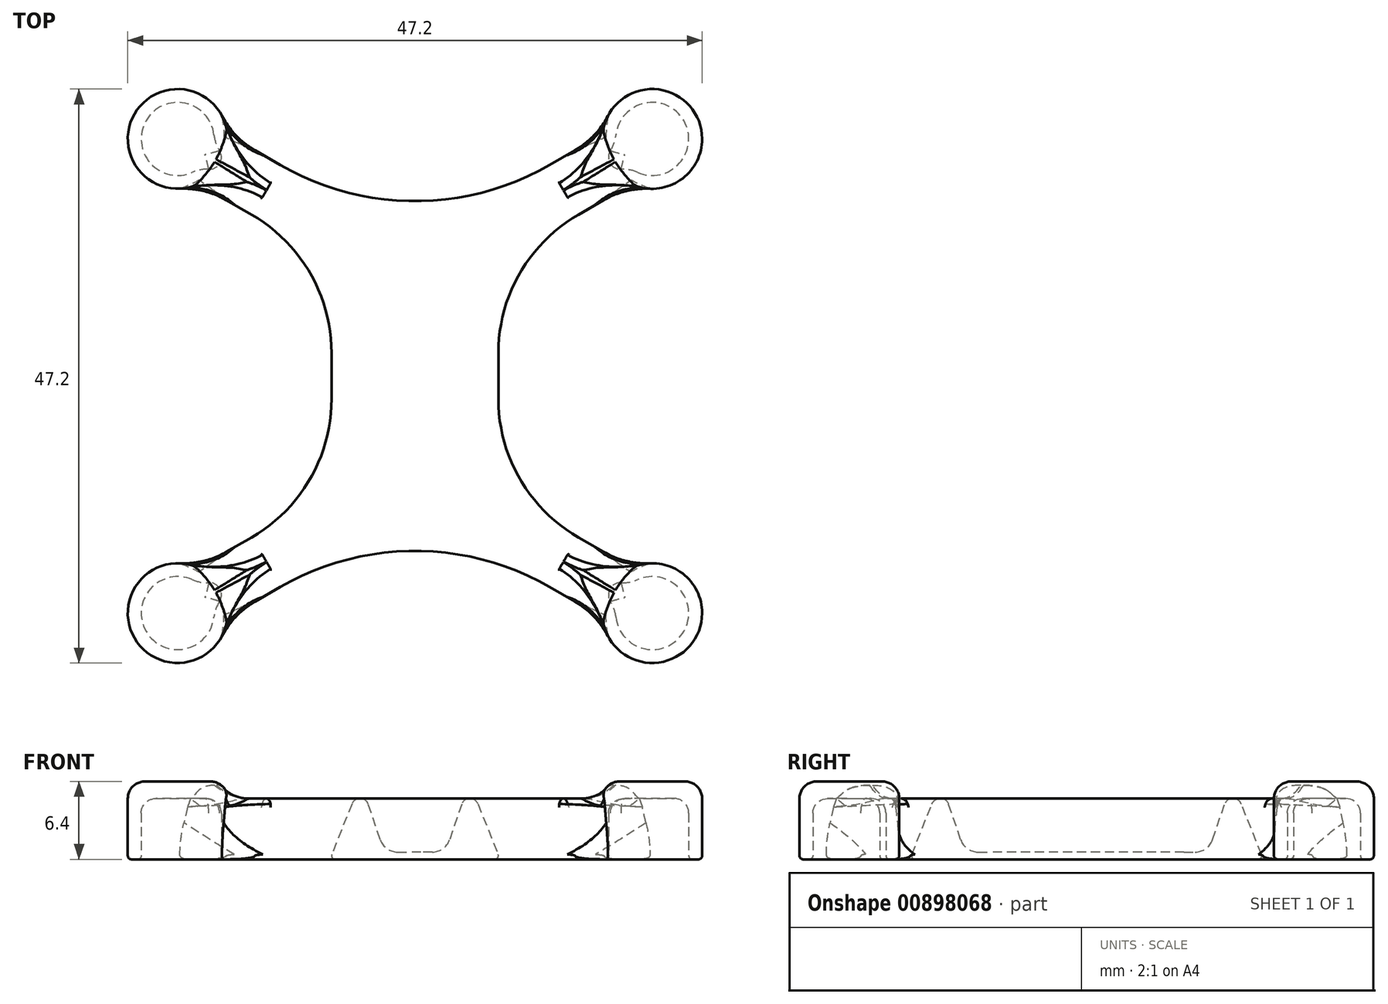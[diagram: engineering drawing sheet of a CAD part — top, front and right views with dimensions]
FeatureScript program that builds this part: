
annotation { "Feature Type Name" : "Feature", "Feature Type Description" : "" }
export const myFeature = defineFeature(function(context is Context, id is Id, definition is map)
    precondition{}
    {
        {
            var Q0;
            Q0=qCreatedBy(makeId("Top.planeOp"),FACE);
            var sketch = newSketch(context, id + "F0", { "sketchPlane" : qUnion([Q0])});
            skLineSegment(sketch, "E0", {"start": v(-15.44, 20.04) * mm, "end": v(0, 11.13) * mm});
            skLineSegment(sketch, "E1", {"start": v(0, 11.13) * mm, "end": v(15.44, 20.04) * mm});
            skLineSegment(sketch, "E2", {"start": v(-15.44, -20.04) * mm, "end": v(0, -11.13) * mm});
            skLineSegment(sketch, "E3", {"start": v(0, -11.13) * mm, "end": v(15.44, -20.04) * mm});
            skLineSegment(sketch, "E4", {"start": v(-17.94, 15.71) * mm, "end": v(-7, 9.4) * mm});
            skLineSegment(sketch, "E5", {"start": v(-7, 9.4) * mm, "end": v(-7, -9.4) * mm});
            skLineSegment(sketch, "E6", {"start": v(-7, -9.4) * mm, "end": v(-17.94, -15.71) * mm});
            skLineSegment(sketch, "E7", {"start": v(17.94, -15.71) * mm, "end": v(7, -9.4) * mm});
            skLineSegment(sketch, "E8", {"start": v(7, -9.4) * mm, "end": v(7, 9.4) * mm});
            skLineSegment(sketch, "E9", {"start": v(7, 9.4) * mm, "end": v(17.94, 15.71) * mm});
            skArc(sketch, "E10", {"start": v(-17.94, 15.71) * mm, "mid": v(-23.05, 21.55) * mm, "end": v(-15.44, 20.04) * mm});
            skArc(sketch, "E11", {"start": v(17.94, 15.71) * mm, "mid": v(23.05, 21.55) * mm, "end": v(15.44, 20.04) * mm});
            skArc(sketch, "E12", {"start": v(17.94, -15.71) * mm, "mid": v(23.05, -21.55) * mm, "end": v(15.44, -20.04) * mm});
            skArc(sketch, "E13", {"start": v(-17.94, -15.71) * mm, "mid": v(-23.05, -21.55) * mm, "end": v(-15.44, -20.04) * mm});
            skArc(sketch, "E14", {"start": v(-16.06, 18.54) * mm, "mid": v(-16.04, 17.5) * mm, "end": v(-16.95, 17) * mm});
            skArc(sketch, "E15", {"start": v(16.06, 18.54) * mm, "mid": v(16.04, 17.5) * mm, "end": v(16.95, 17) * mm});
            skArc(sketch, "E16", {"start": v(-16.95, -17) * mm, "mid": v(-16.04, -17.5) * mm, "end": v(-16.06, -18.54) * mm});
            skArc(sketch, "E17", {"start": v(16.95, -17) * mm, "mid": v(16.04, -17.5) * mm, "end": v(16.06, -18.54) * mm});
            skArc(sketch, "E18", {"start": v(18.3, -16.75) * mm, "mid": v(22.1, -21) * mm, "end": v(16.52, -19.83) * mm});
            skArc(sketch, "E19", {"start": v(-18.3, -16.75) * mm, "mid": v(-22.1, -21) * mm, "end": v(-16.52, -19.83) * mm});
            skArc(sketch, "E20", {"start": v(-16.52, 19.83) * mm, "mid": v(-22.1, 21) * mm, "end": v(-18.3, 16.75) * mm});
            skArc(sketch, "E21", {"start": v(18.3, 16.75) * mm, "mid": v(22.1, 21) * mm, "end": v(16.52, 19.83) * mm});
            skPoint(sketch, "E22.visualSharp", {"position": v(-16.55, 18.94) * mm});
            skArc(sketch, "E22.filletArc", {"start": v(-16.52, 19.83) * mm, "mid": v(-16.36, 19.16) * mm, "end": v(-16.06, 18.54) * mm});
            skPoint(sketch, "E23.visualSharp", {"position": v(-17.54, 17.23) * mm});
            skArc(sketch, "E23.filletArc", {"start": v(-16.95, 17) * mm, "mid": v(-17.64, 16.95) * mm, "end": v(-18.3, 16.75) * mm});
            skPoint(sketch, "E24.visualSharp", {"position": v(16.55, 18.94) * mm});
            skArc(sketch, "E24.filletArc", {"start": v(16.06, 18.54) * mm, "mid": v(16.36, 19.16) * mm, "end": v(16.52, 19.83) * mm});
            skPoint(sketch, "E25.visualSharp", {"position": v(17.54, 17.23) * mm});
            skArc(sketch, "E25.filletArc", {"start": v(18.3, 16.75) * mm, "mid": v(17.64, 16.95) * mm, "end": v(16.95, 17) * mm});
            skPoint(sketch, "E26.visualSharp", {"position": v(17.54, -17.23) * mm});
            skArc(sketch, "E26.filletArc", {"start": v(16.95, -17) * mm, "mid": v(17.64, -16.95) * mm, "end": v(18.3, -16.75) * mm});
            skPoint(sketch, "E27.visualSharp", {"position": v(16.55, -18.94) * mm});
            skArc(sketch, "E27.filletArc", {"start": v(16.52, -19.83) * mm, "mid": v(16.36, -19.16) * mm, "end": v(16.06, -18.54) * mm});
            skPoint(sketch, "E28.visualSharp", {"position": v(-17.54, -17.23) * mm});
            skArc(sketch, "E28.filletArc", {"start": v(-18.3, -16.75) * mm, "mid": v(-17.64, -16.95) * mm, "end": v(-16.95, -17) * mm});
            skPoint(sketch, "E29.visualSharp", {"position": v(-16.55, -18.94) * mm});
            skArc(sketch, "E29.filletArc", {"start": v(-16.06, -18.54) * mm, "mid": v(-16.36, -19.16) * mm, "end": v(-16.52, -19.83) * mm});
            skSolve(sketch);
        }
        {
            var Q0;
            Q0=qSketchRegion(id+"F0",true);
            extrude(context, id + "F1", {"entities" : qUnion([Q0]), "depth" : 5 * mm, "offsetDistance" : 25 * mm});
        }
        {
            var Q0;
            Q0=qCreatedBy(makeId("Front.planeOp"),FACE);
            var sketch = newSketch(context, id + "F2", { "sketchPlane" : qUnion([Q0])});
            skLineSegment(sketch, "E30.bottom", {"start": v(-2.5, 5.6) * mm, "end": v(2.5, 5.6) * mm});
            skLineSegment(sketch, "E30.top", {"start": v(-2.5, 0.6) * mm, "end": v(2.5, 0.6) * mm});
            skLineSegment(sketch, "E30.left", {"start": v(-2.5, 5.6) * mm, "end": v(-2.5, 0.6) * mm});
            skLineSegment(sketch, "E30.right", {"start": v(2.5, 5.6) * mm, "end": v(2.5, 0.6) * mm});
            skSolve(sketch);
        }
        {
            var Q0;
            Q0=qSketchRegion(id+"F2",true);
            extrude(context, id + "F3", {"entities" : qUnion([Q0]), "operationType" : NewBodyOperationType.REMOVE, "oppositeDirection" : true, "depth" : 10 * mm, "offsetDistance" : 25 * mm, "hasSecondDirection" : true, "secondDirectionOppositeDirection" : false, "secondDirectionDepth" : 10 * mm});
        }
        {
            var Q0;
            Q0=makeQuery(id+"F1.opExtrude","CAP_FACE",FACE,{"disambiguationData":[OSD([sQuery(id+"F0.wireOp",EDGE,"E0"),sQuery(id+"F0.wireOp",EDGE,"E1"),sQuery(id+"F0.wireOp",EDGE,"E2"),sQuery(id+"F0.wireOp",EDGE,"E3"),sQuery(id+"F0.wireOp",EDGE,"E4"),sQuery(id+"F0.wireOp",EDGE,"E5"),sQuery(id+"F0.wireOp",EDGE,"E6"),sQuery(id+"F0.wireOp",EDGE,"E7"),sQuery(id+"F0.wireOp",EDGE,"E8"),sQuery(id+"F0.wireOp",EDGE,"E9"),sQuery(id+"F0.wireOp",EDGE,"E10"),sQuery(id+"F0.wireOp",EDGE,"E11"),sQuery(id+"F0.wireOp",EDGE,"E12"),sQuery(id+"F0.wireOp",EDGE,"E13"),sQuery(id+"F0.wireOp",EDGE,"E14"),sQuery(id+"F0.wireOp",EDGE,"E15"),sQuery(id+"F0.wireOp",EDGE,"E16"),sQuery(id+"F0.wireOp",EDGE,"E17"),sQuery(id+"F0.wireOp",EDGE,"E18"),sQuery(id+"F0.wireOp",EDGE,"E19"),sQuery(id+"F0.wireOp",EDGE,"E20"),sQuery(id+"F0.wireOp",EDGE,"E21")])],"isStart":false});
            var sketch = newSketch(context, id + "F4", { "sketchPlane" : qUnion([Q0])});
            skCircle(sketch, "E31", {"center": v(-19.5, 19.5) * mm, "radius": 4.1 * mm});
            skCircle(sketch, "E32", {"center": v(19.5, 19.5) * mm, "radius": 4.1 * mm});
            skCircle(sketch, "E33", {"center": v(19.5, -19.5) * mm, "radius": 4.1 * mm});
            skCircle(sketch, "E34", {"center": v(-19.5, -19.5) * mm, "radius": 4.1 * mm});
            skSolve(sketch);
        }
        {
            var Q0;
            Q0=qSketchRegion(id+"F4",true);
            extrude(context, id + "F5", {"entities" : qUnion([Q0]), "operationType" : NewBodyOperationType.ADD, "depth" : 1.4 * mm, "offsetDistance" : 25 * mm});
        }
        {
            var Q0;
            Q0=makeQuery(id+"F1.opExtrude","SWEPT_EDGE",EDGE,{"disambiguationData":[OSD([sQuery(id+"F0.wireOp",EDGE,"E0"),sQuery(id+"F0.wireOp",EDGE,"E1")])]});
            var Q1;
            Q1=makeQuery(id+"F1.opExtrude","SWEPT_EDGE",EDGE,{"disambiguationData":[OSD([sQuery(id+"F0.wireOp",EDGE,"E2"),sQuery(id+"F0.wireOp",EDGE,"E3")])]});
            fillet(context, id + "F6", {"entities" : qUnion([Q0, Q1]), "radius" : 22 * mm, "tangentPropagation" : true, "allowEdgeOverflow" : false});
        }
        {
            var Q0;
            Q0=makeQuery(id+"F1.opExtrude","SWEPT_EDGE",EDGE,{"disambiguationData":[OSD([sQuery(id+"F0.wireOp",EDGE,"E4"),sQuery(id+"F0.wireOp",EDGE,"E5")])]});
            var Q1;
            Q1=makeQuery(id+"F1.opExtrude","SWEPT_EDGE",EDGE,{"disambiguationData":[OSD([sQuery(id+"F0.wireOp",EDGE,"E5"),sQuery(id+"F0.wireOp",EDGE,"E6")])]});
            var Q2;
            Q2=makeQuery(id+"F1.opExtrude","SWEPT_EDGE",EDGE,{"disambiguationData":[OSD([sQuery(id+"F0.wireOp",EDGE,"E8"),sQuery(id+"F0.wireOp",EDGE,"E9")])]});
            var Q3;
            Q3=makeQuery(id+"F1.opExtrude","SWEPT_EDGE",EDGE,{"disambiguationData":[OSD([sQuery(id+"F0.wireOp",EDGE,"E7"),sQuery(id+"F0.wireOp",EDGE,"E8")])]});
            fillet(context, id + "F7", {"entities" : qUnion([Q0, Q1, Q2, Q3]), "radius" : 13 * mm, "tangentPropagation" : true, "allowEdgeOverflow" : false});
        }
        {
            var Q0;
            Q0=makeQuery(id+"F1.opExtrude","CAP_EDGE",EDGE,{"disambiguationData":[OSD([sQuery(id+"F0.wireOp",EDGE,"E2")])],"isStart":false});
            var Q1;
            Q1=makeQuery(id+"F1.opExtrude","CAP_EDGE",EDGE,{"disambiguationData":[OSD([sQuery(id+"F0.wireOp",EDGE,"E6")])],"isStart":false});
            var Q2;
            Q2=makeQuery(id+"F1.opExtrude","CAP_EDGE",EDGE,{"disambiguationData":[OSD([sQuery(id+"F0.wireOp",EDGE,"E3")])],"isStart":false});
            var Q3;
            Q3=makeQuery(id+"F1.opExtrude","CAP_EDGE",EDGE,{"disambiguationData":[OSD([sQuery(id+"F0.wireOp",EDGE,"E7")])],"isStart":false});
            var Q4;
            Q4=makeQuery(id+"F1.opExtrude","CAP_EDGE",EDGE,{"disambiguationData":[OSD([sQuery(id+"F0.wireOp",EDGE,"E1")])],"isStart":false});
            var Q5;
            Q5=makeQuery(id+"F1.opExtrude","CAP_EDGE",EDGE,{"disambiguationData":[OSD([sQuery(id+"F0.wireOp",EDGE,"E0")])],"isStart":false});
            var Q6;
            Q6=makeQuery(id+"F1.opExtrude","CAP_EDGE",EDGE,{"disambiguationData":[OSD([sQuery(id+"F0.wireOp",EDGE,"E4")])],"isStart":false});
            var Q7;
            Q7=makeQuery(id+"F1.opExtrude","CAP_EDGE",EDGE,{"disambiguationData":[OSD([sQuery(id+"F0.wireOp",EDGE,"E9")])],"isStart":false});
            chamfer(context, id + "F8", {"entities" : qUnion([Q0, Q1, Q2, Q3, Q4, Q5, Q6, Q7]), "chamferType" : ChamferType.TWO_OFFSETS, "width1" : 2 * mm, "oppositeDirection" : false, "width2" : 5 * mm, "tangentPropagation" : true});
        }
        {
            var Q0;
            Q0=makeQuery(id+"F3.boolean.opBoolean","COPY",EDGE,{"derivedFrom":makeQuery(id+"F3.opExtrude","CAP_EDGE",EDGE,{"disambiguationData":[OSD([sQuery(id+"F2.wireOp",EDGE,"E30.left")])],"isStart":false})});
            var Q1;
            Q1=makeQuery(id+"F3.boolean.opBoolean","COPY",EDGE,{"derivedFrom":makeQuery(id+"F3.opExtrude","CAP_EDGE",EDGE,{"disambiguationData":[OSD([sQuery(id+"F2.wireOp",EDGE,"E30.right")])],"isStart":false})});
            var Q2;
            Q2=makeQuery(id+"F3.boolean.opBoolean","COPY",EDGE,{"derivedFrom":makeQuery(id+"F3.opExtrude","CAP_EDGE",EDGE,{"disambiguationData":[OSD([sQuery(id+"F2.wireOp",EDGE,"E30.left")])],"isStart":true})});
            var Q3;
            Q3=makeQuery(id+"F3.boolean.opBoolean","COPY",EDGE,{"derivedFrom":makeQuery(id+"F3.opExtrude","CAP_EDGE",EDGE,{"disambiguationData":[OSD([sQuery(id+"F2.wireOp",EDGE,"E30.right")])],"isStart":true})});
            fillet(context, id + "F9", {"entities" : qUnion([Q0, Q1, Q2, Q3]), "radius" : 2 * mm, "tangentPropagation" : true, "allowEdgeOverflow" : false});
        }
        {
            var Q0;
            Q0=makeQuery(id+"F3.boolean.opBoolean","INTERSECT",EDGE,{"derivedFrom":[makeQuery(id+"F1.opExtrude","CAP_FACE",FACE,{"disambiguationData":[OSD([sQuery(id+"F0.wireOp",EDGE,"E0"),sQuery(id+"F0.wireOp",EDGE,"E1"),sQuery(id+"F0.wireOp",EDGE,"E2"),sQuery(id+"F0.wireOp",EDGE,"E3"),sQuery(id+"F0.wireOp",EDGE,"E4"),sQuery(id+"F0.wireOp",EDGE,"E5"),sQuery(id+"F0.wireOp",EDGE,"E6"),sQuery(id+"F0.wireOp",EDGE,"E7"),sQuery(id+"F0.wireOp",EDGE,"E8"),sQuery(id+"F0.wireOp",EDGE,"E9"),sQuery(id+"F0.wireOp",EDGE,"E10"),sQuery(id+"F0.wireOp",EDGE,"E11"),sQuery(id+"F0.wireOp",EDGE,"E12"),sQuery(id+"F0.wireOp",EDGE,"E13"),sQuery(id+"F0.wireOp",EDGE,"E14"),sQuery(id+"F0.wireOp",EDGE,"E15"),sQuery(id+"F0.wireOp",EDGE,"E16"),sQuery(id+"F0.wireOp",EDGE,"E17"),sQuery(id+"F0.wireOp",EDGE,"E18"),sQuery(id+"F0.wireOp",EDGE,"E19"),sQuery(id+"F0.wireOp",EDGE,"E20"),sQuery(id+"F0.wireOp",EDGE,"E21"),sQuery(id+"F0.wireOp",EDGE,"E22.filletArc"),sQuery(id+"F0.wireOp",EDGE,"E23.filletArc"),sQuery(id+"F0.wireOp",EDGE,"E24.filletArc"),sQuery(id+"F0.wireOp",EDGE,"E25.filletArc"),sQuery(id+"F0.wireOp",EDGE,"E26.filletArc"),sQuery(id+"F0.wireOp",EDGE,"E27.filletArc"),sQuery(id+"F0.wireOp",EDGE,"E28.filletArc"),sQuery(id+"F0.wireOp",EDGE,"E29.filletArc")])],"isStart":false}),makeQuery(id+"F3.opExtrude","CAP_FACE",FACE,{"disambiguationData":[OSD([sQuery(id+"F2.wireOp",EDGE,"E30.bottom"),sQuery(id+"F2.wireOp",EDGE,"E30.top"),sQuery(id+"F2.wireOp",EDGE,"E30.left"),sQuery(id+"F2.wireOp",EDGE,"E30.right")])],"isStart":false})]});
            chamfer(context, id + "F10", {"entities" : qUnion([Q0]), "chamferType" : ChamferType.TWO_OFFSETS, "width1" : 1.5 * mm, "oppositeDirection" : false, "width2" : 4.4 * mm, "tangentPropagation" : true});
        }
        {
            var Q0;
            Q0=makeQuery(id+"F5.opExtrude","CAP_FACE",FACE,{"disambiguationData":[OSD([sQuery(id+"F4.wireOp",EDGE,"E34")])],"isStart":true});
            var Q1;
            Q1=makeQuery(id+"F5.opExtrude","CAP_FACE",FACE,{"disambiguationData":[OSD([sQuery(id+"F4.wireOp",EDGE,"E33")])],"isStart":true});
            var Q2;
            Q2=makeQuery(id+"F5.opExtrude","CAP_FACE",FACE,{"disambiguationData":[OSD([sQuery(id+"F4.wireOp",EDGE,"E32")])],"isStart":true});
            var Q3;
            Q3=makeQuery(id+"F5.opExtrude","CAP_FACE",FACE,{"disambiguationData":[OSD([sQuery(id+"F4.wireOp",EDGE,"E31")])],"isStart":true});
            fillet(context, id + "F11", {"entities" : qUnion([Q0, Q1, Q2, Q3]), "radius" : 1.2 * mm, "tangentPropagation" : true, "allowEdgeOverflow" : false});
        }
        {
            var Q0;
            Q0=makeQuery(id+"F1.opExtrude","CAP_FACE",FACE,{"disambiguationData":[OSD([sQuery(id+"F0.wireOp",EDGE,"E0"),sQuery(id+"F0.wireOp",EDGE,"E1"),sQuery(id+"F0.wireOp",EDGE,"E2"),sQuery(id+"F0.wireOp",EDGE,"E3"),sQuery(id+"F0.wireOp",EDGE,"E4"),sQuery(id+"F0.wireOp",EDGE,"E5"),sQuery(id+"F0.wireOp",EDGE,"E6"),sQuery(id+"F0.wireOp",EDGE,"E7"),sQuery(id+"F0.wireOp",EDGE,"E8"),sQuery(id+"F0.wireOp",EDGE,"E9"),sQuery(id+"F0.wireOp",EDGE,"E10"),sQuery(id+"F0.wireOp",EDGE,"E11"),sQuery(id+"F0.wireOp",EDGE,"E12"),sQuery(id+"F0.wireOp",EDGE,"E13"),sQuery(id+"F0.wireOp",EDGE,"E14"),sQuery(id+"F0.wireOp",EDGE,"E15"),sQuery(id+"F0.wireOp",EDGE,"E16"),sQuery(id+"F0.wireOp",EDGE,"E17"),sQuery(id+"F0.wireOp",EDGE,"E18"),sQuery(id+"F0.wireOp",EDGE,"E19"),sQuery(id+"F0.wireOp",EDGE,"E20"),sQuery(id+"F0.wireOp",EDGE,"E21"),sQuery(id+"F0.wireOp",EDGE,"E22.filletArc"),sQuery(id+"F0.wireOp",EDGE,"E23.filletArc"),sQuery(id+"F0.wireOp",EDGE,"E24.filletArc"),sQuery(id+"F0.wireOp",EDGE,"E25.filletArc"),sQuery(id+"F0.wireOp",EDGE,"E26.filletArc"),sQuery(id+"F0.wireOp",EDGE,"E27.filletArc"),sQuery(id+"F0.wireOp",EDGE,"E28.filletArc"),sQuery(id+"F0.wireOp",EDGE,"E29.filletArc")])],"isStart":true});
            var Q1;
            {var subQ0=sQuery(id+"F0.wireOp",EDGE,"E3");var subQ1=sQuery(id+"F0.wireOp",EDGE,"E2");Q1=makeQuery(id+"F8.opChamfer","BLEND_EDGE",EDGE,{"blendedFrom":[makeQuery(id+"F6.opFillet","BLEND_EDGE",EDGE,{"blendedFrom":[makeQuery(id+"F1.opExtrude","SWEPT_EDGE",EDGE,{"disambiguationData":[OSD([subQ1,subQ0])]}),makeQuery(id+"F1.opExtrude","CAP_FACE",FACE,{"disambiguationData":[OSD([sQuery(id+"F0.wireOp",EDGE,"E0"),sQuery(id+"F0.wireOp",EDGE,"E1"),subQ1,subQ0,sQuery(id+"F0.wireOp",EDGE,"E4"),sQuery(id+"F0.wireOp",EDGE,"E5"),sQuery(id+"F0.wireOp",EDGE,"E6"),sQuery(id+"F0.wireOp",EDGE,"E7"),sQuery(id+"F0.wireOp",EDGE,"E8"),sQuery(id+"F0.wireOp",EDGE,"E9"),sQuery(id+"F0.wireOp",EDGE,"E10"),sQuery(id+"F0.wireOp",EDGE,"E11"),sQuery(id+"F0.wireOp",EDGE,"E12"),sQuery(id+"F0.wireOp",EDGE,"E13"),sQuery(id+"F0.wireOp",EDGE,"E14"),sQuery(id+"F0.wireOp",EDGE,"E15"),sQuery(id+"F0.wireOp",EDGE,"E16"),sQuery(id+"F0.wireOp",EDGE,"E17"),sQuery(id+"F0.wireOp",EDGE,"E18"),sQuery(id+"F0.wireOp",EDGE,"E19"),sQuery(id+"F0.wireOp",EDGE,"E20"),sQuery(id+"F0.wireOp",EDGE,"E21"),sQuery(id+"F0.wireOp",EDGE,"E22.filletArc"),sQuery(id+"F0.wireOp",EDGE,"E23.filletArc"),sQuery(id+"F0.wireOp",EDGE,"E24.filletArc"),sQuery(id+"F0.wireOp",EDGE,"E25.filletArc"),sQuery(id+"F0.wireOp",EDGE,"E26.filletArc"),sQuery(id+"F0.wireOp",EDGE,"E27.filletArc"),sQuery(id+"F0.wireOp",EDGE,"E28.filletArc"),sQuery(id+"F0.wireOp",EDGE,"E29.filletArc")])],"isStart":false})],"blendedInto":[makeQuery(id+"F1.opExtrude","CAP_FACE",FACE,{"disambiguationData":[OSD([sQuery(id+"F0.wireOp",EDGE,"E0"),sQuery(id+"F0.wireOp",EDGE,"E1"),subQ1,subQ0,sQuery(id+"F0.wireOp",EDGE,"E4"),sQuery(id+"F0.wireOp",EDGE,"E5"),sQuery(id+"F0.wireOp",EDGE,"E6"),sQuery(id+"F0.wireOp",EDGE,"E7"),sQuery(id+"F0.wireOp",EDGE,"E8"),sQuery(id+"F0.wireOp",EDGE,"E9"),sQuery(id+"F0.wireOp",EDGE,"E10"),sQuery(id+"F0.wireOp",EDGE,"E11"),sQuery(id+"F0.wireOp",EDGE,"E12"),sQuery(id+"F0.wireOp",EDGE,"E13"),sQuery(id+"F0.wireOp",EDGE,"E14"),sQuery(id+"F0.wireOp",EDGE,"E15"),sQuery(id+"F0.wireOp",EDGE,"E16"),sQuery(id+"F0.wireOp",EDGE,"E17"),sQuery(id+"F0.wireOp",EDGE,"E18"),sQuery(id+"F0.wireOp",EDGE,"E19"),sQuery(id+"F0.wireOp",EDGE,"E20"),sQuery(id+"F0.wireOp",EDGE,"E21"),sQuery(id+"F0.wireOp",EDGE,"E22.filletArc"),sQuery(id+"F0.wireOp",EDGE,"E23.filletArc"),sQuery(id+"F0.wireOp",EDGE,"E24.filletArc"),sQuery(id+"F0.wireOp",EDGE,"E25.filletArc"),sQuery(id+"F0.wireOp",EDGE,"E26.filletArc"),sQuery(id+"F0.wireOp",EDGE,"E27.filletArc"),sQuery(id+"F0.wireOp",EDGE,"E28.filletArc"),sQuery(id+"F0.wireOp",EDGE,"E29.filletArc")])],"isStart":false})]}),makeQuery(id+"F6.opFillet","BLEND_FACE",FACE,{"disambiguationData":[OSD([subQ1,subQ0])]})],"blendedInto":[makeQuery(id+"F6.opFillet","BLEND_FACE",FACE,{"disambiguationData":[OSD([subQ1,subQ0])]})]});}
            var Q2;
            {var subQ0=sQuery(id+"F0.wireOp",EDGE,"E5");var subQ1=sQuery(id+"F0.wireOp",EDGE,"E4");Q2=makeQuery(id+"F8.opChamfer","BLEND_EDGE",EDGE,{"blendedFrom":[makeQuery(id+"F7.opFillet","BLEND_EDGE",EDGE,{"blendedFrom":[makeQuery(id+"F1.opExtrude","SWEPT_EDGE",EDGE,{"disambiguationData":[OSD([subQ1,subQ0])]}),makeQuery(id+"F1.opExtrude","CAP_FACE",FACE,{"disambiguationData":[OSD([sQuery(id+"F0.wireOp",EDGE,"E0"),sQuery(id+"F0.wireOp",EDGE,"E1"),sQuery(id+"F0.wireOp",EDGE,"E2"),sQuery(id+"F0.wireOp",EDGE,"E3"),subQ1,subQ0,sQuery(id+"F0.wireOp",EDGE,"E6"),sQuery(id+"F0.wireOp",EDGE,"E7"),sQuery(id+"F0.wireOp",EDGE,"E8"),sQuery(id+"F0.wireOp",EDGE,"E9"),sQuery(id+"F0.wireOp",EDGE,"E10"),sQuery(id+"F0.wireOp",EDGE,"E11"),sQuery(id+"F0.wireOp",EDGE,"E12"),sQuery(id+"F0.wireOp",EDGE,"E13"),sQuery(id+"F0.wireOp",EDGE,"E14"),sQuery(id+"F0.wireOp",EDGE,"E15"),sQuery(id+"F0.wireOp",EDGE,"E16"),sQuery(id+"F0.wireOp",EDGE,"E17"),sQuery(id+"F0.wireOp",EDGE,"E18"),sQuery(id+"F0.wireOp",EDGE,"E19"),sQuery(id+"F0.wireOp",EDGE,"E20"),sQuery(id+"F0.wireOp",EDGE,"E21"),sQuery(id+"F0.wireOp",EDGE,"E22.filletArc"),sQuery(id+"F0.wireOp",EDGE,"E23.filletArc"),sQuery(id+"F0.wireOp",EDGE,"E24.filletArc"),sQuery(id+"F0.wireOp",EDGE,"E25.filletArc"),sQuery(id+"F0.wireOp",EDGE,"E26.filletArc"),sQuery(id+"F0.wireOp",EDGE,"E27.filletArc"),sQuery(id+"F0.wireOp",EDGE,"E28.filletArc"),sQuery(id+"F0.wireOp",EDGE,"E29.filletArc")])],"isStart":false})],"blendedInto":[makeQuery(id+"F1.opExtrude","CAP_FACE",FACE,{"disambiguationData":[OSD([sQuery(id+"F0.wireOp",EDGE,"E0"),sQuery(id+"F0.wireOp",EDGE,"E1"),sQuery(id+"F0.wireOp",EDGE,"E2"),sQuery(id+"F0.wireOp",EDGE,"E3"),subQ1,subQ0,sQuery(id+"F0.wireOp",EDGE,"E6"),sQuery(id+"F0.wireOp",EDGE,"E7"),sQuery(id+"F0.wireOp",EDGE,"E8"),sQuery(id+"F0.wireOp",EDGE,"E9"),sQuery(id+"F0.wireOp",EDGE,"E10"),sQuery(id+"F0.wireOp",EDGE,"E11"),sQuery(id+"F0.wireOp",EDGE,"E12"),sQuery(id+"F0.wireOp",EDGE,"E13"),sQuery(id+"F0.wireOp",EDGE,"E14"),sQuery(id+"F0.wireOp",EDGE,"E15"),sQuery(id+"F0.wireOp",EDGE,"E16"),sQuery(id+"F0.wireOp",EDGE,"E17"),sQuery(id+"F0.wireOp",EDGE,"E18"),sQuery(id+"F0.wireOp",EDGE,"E19"),sQuery(id+"F0.wireOp",EDGE,"E20"),sQuery(id+"F0.wireOp",EDGE,"E21"),sQuery(id+"F0.wireOp",EDGE,"E22.filletArc"),sQuery(id+"F0.wireOp",EDGE,"E23.filletArc"),sQuery(id+"F0.wireOp",EDGE,"E24.filletArc"),sQuery(id+"F0.wireOp",EDGE,"E25.filletArc"),sQuery(id+"F0.wireOp",EDGE,"E26.filletArc"),sQuery(id+"F0.wireOp",EDGE,"E27.filletArc"),sQuery(id+"F0.wireOp",EDGE,"E28.filletArc"),sQuery(id+"F0.wireOp",EDGE,"E29.filletArc")])],"isStart":false})]}),makeQuery(id+"F7.opFillet","BLEND_FACE",FACE,{"disambiguationData":[OSD([subQ1,subQ0])]})],"blendedInto":[makeQuery(id+"F7.opFillet","BLEND_FACE",FACE,{"disambiguationData":[OSD([subQ1,subQ0])]})]});}
            var Q3;
            {var subQ0=sQuery(id+"F0.wireOp",EDGE,"E9");var subQ1=sQuery(id+"F0.wireOp",EDGE,"E8");Q3=makeQuery(id+"F8.opChamfer","BLEND_EDGE",EDGE,{"blendedFrom":[makeQuery(id+"F7.opFillet","BLEND_EDGE",EDGE,{"blendedFrom":[makeQuery(id+"F1.opExtrude","SWEPT_EDGE",EDGE,{"disambiguationData":[OSD([subQ1,subQ0])]}),makeQuery(id+"F1.opExtrude","CAP_FACE",FACE,{"disambiguationData":[OSD([sQuery(id+"F0.wireOp",EDGE,"E0"),sQuery(id+"F0.wireOp",EDGE,"E1"),sQuery(id+"F0.wireOp",EDGE,"E2"),sQuery(id+"F0.wireOp",EDGE,"E3"),sQuery(id+"F0.wireOp",EDGE,"E4"),sQuery(id+"F0.wireOp",EDGE,"E5"),sQuery(id+"F0.wireOp",EDGE,"E6"),sQuery(id+"F0.wireOp",EDGE,"E7"),subQ1,subQ0,sQuery(id+"F0.wireOp",EDGE,"E10"),sQuery(id+"F0.wireOp",EDGE,"E11"),sQuery(id+"F0.wireOp",EDGE,"E12"),sQuery(id+"F0.wireOp",EDGE,"E13"),sQuery(id+"F0.wireOp",EDGE,"E14"),sQuery(id+"F0.wireOp",EDGE,"E15"),sQuery(id+"F0.wireOp",EDGE,"E16"),sQuery(id+"F0.wireOp",EDGE,"E17"),sQuery(id+"F0.wireOp",EDGE,"E18"),sQuery(id+"F0.wireOp",EDGE,"E19"),sQuery(id+"F0.wireOp",EDGE,"E20"),sQuery(id+"F0.wireOp",EDGE,"E21"),sQuery(id+"F0.wireOp",EDGE,"E22.filletArc"),sQuery(id+"F0.wireOp",EDGE,"E23.filletArc"),sQuery(id+"F0.wireOp",EDGE,"E24.filletArc"),sQuery(id+"F0.wireOp",EDGE,"E25.filletArc"),sQuery(id+"F0.wireOp",EDGE,"E26.filletArc"),sQuery(id+"F0.wireOp",EDGE,"E27.filletArc"),sQuery(id+"F0.wireOp",EDGE,"E28.filletArc"),sQuery(id+"F0.wireOp",EDGE,"E29.filletArc")])],"isStart":false})],"blendedInto":[makeQuery(id+"F1.opExtrude","CAP_FACE",FACE,{"disambiguationData":[OSD([sQuery(id+"F0.wireOp",EDGE,"E0"),sQuery(id+"F0.wireOp",EDGE,"E1"),sQuery(id+"F0.wireOp",EDGE,"E2"),sQuery(id+"F0.wireOp",EDGE,"E3"),sQuery(id+"F0.wireOp",EDGE,"E4"),sQuery(id+"F0.wireOp",EDGE,"E5"),sQuery(id+"F0.wireOp",EDGE,"E6"),sQuery(id+"F0.wireOp",EDGE,"E7"),subQ1,subQ0,sQuery(id+"F0.wireOp",EDGE,"E10"),sQuery(id+"F0.wireOp",EDGE,"E11"),sQuery(id+"F0.wireOp",EDGE,"E12"),sQuery(id+"F0.wireOp",EDGE,"E13"),sQuery(id+"F0.wireOp",EDGE,"E14"),sQuery(id+"F0.wireOp",EDGE,"E15"),sQuery(id+"F0.wireOp",EDGE,"E16"),sQuery(id+"F0.wireOp",EDGE,"E17"),sQuery(id+"F0.wireOp",EDGE,"E18"),sQuery(id+"F0.wireOp",EDGE,"E19"),sQuery(id+"F0.wireOp",EDGE,"E20"),sQuery(id+"F0.wireOp",EDGE,"E21"),sQuery(id+"F0.wireOp",EDGE,"E22.filletArc"),sQuery(id+"F0.wireOp",EDGE,"E23.filletArc"),sQuery(id+"F0.wireOp",EDGE,"E24.filletArc"),sQuery(id+"F0.wireOp",EDGE,"E25.filletArc"),sQuery(id+"F0.wireOp",EDGE,"E26.filletArc"),sQuery(id+"F0.wireOp",EDGE,"E27.filletArc"),sQuery(id+"F0.wireOp",EDGE,"E28.filletArc"),sQuery(id+"F0.wireOp",EDGE,"E29.filletArc")])],"isStart":false})]}),makeQuery(id+"F7.opFillet","BLEND_FACE",FACE,{"disambiguationData":[OSD([subQ1,subQ0])]})],"blendedInto":[makeQuery(id+"F7.opFillet","BLEND_FACE",FACE,{"disambiguationData":[OSD([subQ1,subQ0])]})]});}
            var Q4;
            {var subQ0=sQuery(id+"F0.wireOp",EDGE,"E1");var subQ1=sQuery(id+"F0.wireOp",EDGE,"E0");Q4=makeQuery(id+"F8.opChamfer","BLEND_EDGE",EDGE,{"blendedFrom":[makeQuery(id+"F6.opFillet","BLEND_EDGE",EDGE,{"blendedFrom":[makeQuery(id+"F1.opExtrude","SWEPT_EDGE",EDGE,{"disambiguationData":[OSD([subQ1,subQ0])]}),makeQuery(id+"F1.opExtrude","CAP_FACE",FACE,{"disambiguationData":[OSD([subQ1,subQ0,sQuery(id+"F0.wireOp",EDGE,"E2"),sQuery(id+"F0.wireOp",EDGE,"E3"),sQuery(id+"F0.wireOp",EDGE,"E4"),sQuery(id+"F0.wireOp",EDGE,"E5"),sQuery(id+"F0.wireOp",EDGE,"E6"),sQuery(id+"F0.wireOp",EDGE,"E7"),sQuery(id+"F0.wireOp",EDGE,"E8"),sQuery(id+"F0.wireOp",EDGE,"E9"),sQuery(id+"F0.wireOp",EDGE,"E10"),sQuery(id+"F0.wireOp",EDGE,"E11"),sQuery(id+"F0.wireOp",EDGE,"E12"),sQuery(id+"F0.wireOp",EDGE,"E13"),sQuery(id+"F0.wireOp",EDGE,"E14"),sQuery(id+"F0.wireOp",EDGE,"E15"),sQuery(id+"F0.wireOp",EDGE,"E16"),sQuery(id+"F0.wireOp",EDGE,"E17"),sQuery(id+"F0.wireOp",EDGE,"E18"),sQuery(id+"F0.wireOp",EDGE,"E19"),sQuery(id+"F0.wireOp",EDGE,"E20"),sQuery(id+"F0.wireOp",EDGE,"E21"),sQuery(id+"F0.wireOp",EDGE,"E22.filletArc"),sQuery(id+"F0.wireOp",EDGE,"E23.filletArc"),sQuery(id+"F0.wireOp",EDGE,"E24.filletArc"),sQuery(id+"F0.wireOp",EDGE,"E25.filletArc"),sQuery(id+"F0.wireOp",EDGE,"E26.filletArc"),sQuery(id+"F0.wireOp",EDGE,"E27.filletArc"),sQuery(id+"F0.wireOp",EDGE,"E28.filletArc"),sQuery(id+"F0.wireOp",EDGE,"E29.filletArc")])],"isStart":false})],"blendedInto":[makeQuery(id+"F1.opExtrude","CAP_FACE",FACE,{"disambiguationData":[OSD([subQ1,subQ0,sQuery(id+"F0.wireOp",EDGE,"E2"),sQuery(id+"F0.wireOp",EDGE,"E3"),sQuery(id+"F0.wireOp",EDGE,"E4"),sQuery(id+"F0.wireOp",EDGE,"E5"),sQuery(id+"F0.wireOp",EDGE,"E6"),sQuery(id+"F0.wireOp",EDGE,"E7"),sQuery(id+"F0.wireOp",EDGE,"E8"),sQuery(id+"F0.wireOp",EDGE,"E9"),sQuery(id+"F0.wireOp",EDGE,"E10"),sQuery(id+"F0.wireOp",EDGE,"E11"),sQuery(id+"F0.wireOp",EDGE,"E12"),sQuery(id+"F0.wireOp",EDGE,"E13"),sQuery(id+"F0.wireOp",EDGE,"E14"),sQuery(id+"F0.wireOp",EDGE,"E15"),sQuery(id+"F0.wireOp",EDGE,"E16"),sQuery(id+"F0.wireOp",EDGE,"E17"),sQuery(id+"F0.wireOp",EDGE,"E18"),sQuery(id+"F0.wireOp",EDGE,"E19"),sQuery(id+"F0.wireOp",EDGE,"E20"),sQuery(id+"F0.wireOp",EDGE,"E21"),sQuery(id+"F0.wireOp",EDGE,"E22.filletArc"),sQuery(id+"F0.wireOp",EDGE,"E23.filletArc"),sQuery(id+"F0.wireOp",EDGE,"E24.filletArc"),sQuery(id+"F0.wireOp",EDGE,"E25.filletArc"),sQuery(id+"F0.wireOp",EDGE,"E26.filletArc"),sQuery(id+"F0.wireOp",EDGE,"E27.filletArc"),sQuery(id+"F0.wireOp",EDGE,"E28.filletArc"),sQuery(id+"F0.wireOp",EDGE,"E29.filletArc")])],"isStart":false})]}),makeQuery(id+"F6.opFillet","BLEND_FACE",FACE,{"disambiguationData":[OSD([subQ1,subQ0])]})],"blendedInto":[makeQuery(id+"F6.opFillet","BLEND_FACE",FACE,{"disambiguationData":[OSD([subQ1,subQ0])]})]});}
            fillet(context, id + "F12", {"entities" : qUnion([Q0, Q1, Q2, Q3, Q4]), "radius" : .3 * mm, "tangentPropagation" : true, "allowEdgeOverflow" : false});
        }
        {
            var Q0;
            Q0=makeQuery(id+"F8.opChamfer","BLEND_EDGE",EDGE,{"blendedFrom":[makeQuery(id+"F1.opExtrude","CAP_EDGE",EDGE,{"disambiguationData":[OSD([sQuery(id+"F0.wireOp",EDGE,"E2")])],"isStart":false}),makeQuery(id+"F5.boolean.opBoolean","MERGE",FACE,{"derivedFrom":[makeQuery(id+"F1.opExtrude","SWEPT_FACE",FACE,{"disambiguationData":[OSD([sQuery(id+"F0.wireOp",EDGE,"E13")])]}),makeQuery(id+"F5.opExtrude","SWEPT_FACE",FACE,{"disambiguationData":[OSD([sQuery(id+"F4.wireOp",EDGE,"E34")])]})]})],"blendedInto":[makeQuery(id+"F5.boolean.opBoolean","MERGE",FACE,{"derivedFrom":[makeQuery(id+"F1.opExtrude","SWEPT_FACE",FACE,{"disambiguationData":[OSD([sQuery(id+"F0.wireOp",EDGE,"E13")])]}),makeQuery(id+"F5.opExtrude","SWEPT_FACE",FACE,{"disambiguationData":[OSD([sQuery(id+"F4.wireOp",EDGE,"E34")])]})]})]});
            var Q1;
            Q1=makeQuery(id+"F8.opChamfer","BLEND_EDGE",EDGE,{"blendedFrom":[makeQuery(id+"F1.opExtrude","CAP_EDGE",EDGE,{"disambiguationData":[OSD([sQuery(id+"F0.wireOp",EDGE,"E6")])],"isStart":false}),makeQuery(id+"F5.boolean.opBoolean","MERGE",FACE,{"derivedFrom":[makeQuery(id+"F1.opExtrude","SWEPT_FACE",FACE,{"disambiguationData":[OSD([sQuery(id+"F0.wireOp",EDGE,"E13")])]}),makeQuery(id+"F5.opExtrude","SWEPT_FACE",FACE,{"disambiguationData":[OSD([sQuery(id+"F4.wireOp",EDGE,"E34")])]})]})],"blendedInto":[makeQuery(id+"F5.boolean.opBoolean","MERGE",FACE,{"derivedFrom":[makeQuery(id+"F1.opExtrude","SWEPT_FACE",FACE,{"disambiguationData":[OSD([sQuery(id+"F0.wireOp",EDGE,"E13")])]}),makeQuery(id+"F5.opExtrude","SWEPT_FACE",FACE,{"disambiguationData":[OSD([sQuery(id+"F4.wireOp",EDGE,"E34")])]})]})]});
            var Q2;
            Q2=makeQuery(id+"F8.opChamfer","BLEND_EDGE",EDGE,{"blendedFrom":[makeQuery(id+"F1.opExtrude","CAP_EDGE",EDGE,{"disambiguationData":[OSD([sQuery(id+"F0.wireOp",EDGE,"E3")])],"isStart":false}),makeQuery(id+"F5.boolean.opBoolean","MERGE",FACE,{"derivedFrom":[makeQuery(id+"F1.opExtrude","SWEPT_FACE",FACE,{"disambiguationData":[OSD([sQuery(id+"F0.wireOp",EDGE,"E12")])]}),makeQuery(id+"F5.opExtrude","SWEPT_FACE",FACE,{"disambiguationData":[OSD([sQuery(id+"F4.wireOp",EDGE,"E33")])]})]})],"blendedInto":[makeQuery(id+"F5.boolean.opBoolean","MERGE",FACE,{"derivedFrom":[makeQuery(id+"F1.opExtrude","SWEPT_FACE",FACE,{"disambiguationData":[OSD([sQuery(id+"F0.wireOp",EDGE,"E12")])]}),makeQuery(id+"F5.opExtrude","SWEPT_FACE",FACE,{"disambiguationData":[OSD([sQuery(id+"F4.wireOp",EDGE,"E33")])]})]})]});
            var Q3;
            Q3=makeQuery(id+"F8.opChamfer","BLEND_EDGE",EDGE,{"blendedFrom":[makeQuery(id+"F1.opExtrude","CAP_EDGE",EDGE,{"disambiguationData":[OSD([sQuery(id+"F0.wireOp",EDGE,"E7")])],"isStart":false}),makeQuery(id+"F5.boolean.opBoolean","MERGE",FACE,{"derivedFrom":[makeQuery(id+"F1.opExtrude","SWEPT_FACE",FACE,{"disambiguationData":[OSD([sQuery(id+"F0.wireOp",EDGE,"E12")])]}),makeQuery(id+"F5.opExtrude","SWEPT_FACE",FACE,{"disambiguationData":[OSD([sQuery(id+"F4.wireOp",EDGE,"E33")])]})]})],"blendedInto":[makeQuery(id+"F5.boolean.opBoolean","MERGE",FACE,{"derivedFrom":[makeQuery(id+"F1.opExtrude","SWEPT_FACE",FACE,{"disambiguationData":[OSD([sQuery(id+"F0.wireOp",EDGE,"E12")])]}),makeQuery(id+"F5.opExtrude","SWEPT_FACE",FACE,{"disambiguationData":[OSD([sQuery(id+"F4.wireOp",EDGE,"E33")])]})]})]});
            var Q4;
            Q4=makeQuery(id+"F8.opChamfer","BLEND_EDGE",EDGE,{"blendedFrom":[makeQuery(id+"F1.opExtrude","CAP_EDGE",EDGE,{"disambiguationData":[OSD([sQuery(id+"F0.wireOp",EDGE,"E9")])],"isStart":false}),makeQuery(id+"F5.boolean.opBoolean","MERGE",FACE,{"derivedFrom":[makeQuery(id+"F1.opExtrude","SWEPT_FACE",FACE,{"disambiguationData":[OSD([sQuery(id+"F0.wireOp",EDGE,"E11")])]}),makeQuery(id+"F5.opExtrude","SWEPT_FACE",FACE,{"disambiguationData":[OSD([sQuery(id+"F4.wireOp",EDGE,"E32")])]})]})],"blendedInto":[makeQuery(id+"F5.boolean.opBoolean","MERGE",FACE,{"derivedFrom":[makeQuery(id+"F1.opExtrude","SWEPT_FACE",FACE,{"disambiguationData":[OSD([sQuery(id+"F0.wireOp",EDGE,"E11")])]}),makeQuery(id+"F5.opExtrude","SWEPT_FACE",FACE,{"disambiguationData":[OSD([sQuery(id+"F4.wireOp",EDGE,"E32")])]})]})]});
            var Q5;
            Q5=makeQuery(id+"F8.opChamfer","BLEND_EDGE",EDGE,{"blendedFrom":[makeQuery(id+"F1.opExtrude","CAP_EDGE",EDGE,{"disambiguationData":[OSD([sQuery(id+"F0.wireOp",EDGE,"E4")])],"isStart":false}),makeQuery(id+"F5.boolean.opBoolean","MERGE",FACE,{"derivedFrom":[makeQuery(id+"F1.opExtrude","SWEPT_FACE",FACE,{"disambiguationData":[OSD([sQuery(id+"F0.wireOp",EDGE,"E10")])]}),makeQuery(id+"F5.opExtrude","SWEPT_FACE",FACE,{"disambiguationData":[OSD([sQuery(id+"F4.wireOp",EDGE,"E31")])]})]})],"blendedInto":[makeQuery(id+"F5.boolean.opBoolean","MERGE",FACE,{"derivedFrom":[makeQuery(id+"F1.opExtrude","SWEPT_FACE",FACE,{"disambiguationData":[OSD([sQuery(id+"F0.wireOp",EDGE,"E10")])]}),makeQuery(id+"F5.opExtrude","SWEPT_FACE",FACE,{"disambiguationData":[OSD([sQuery(id+"F4.wireOp",EDGE,"E31")])]})]})]});
            var Q6;
            Q6=makeQuery(id+"F8.opChamfer","BLEND_EDGE",EDGE,{"blendedFrom":[makeQuery(id+"F1.opExtrude","CAP_EDGE",EDGE,{"disambiguationData":[OSD([sQuery(id+"F0.wireOp",EDGE,"E0")])],"isStart":false}),makeQuery(id+"F5.boolean.opBoolean","MERGE",FACE,{"derivedFrom":[makeQuery(id+"F1.opExtrude","SWEPT_FACE",FACE,{"disambiguationData":[OSD([sQuery(id+"F0.wireOp",EDGE,"E10")])]}),makeQuery(id+"F5.opExtrude","SWEPT_FACE",FACE,{"disambiguationData":[OSD([sQuery(id+"F4.wireOp",EDGE,"E31")])]})]})],"blendedInto":[makeQuery(id+"F5.boolean.opBoolean","MERGE",FACE,{"derivedFrom":[makeQuery(id+"F1.opExtrude","SWEPT_FACE",FACE,{"disambiguationData":[OSD([sQuery(id+"F0.wireOp",EDGE,"E10")])]}),makeQuery(id+"F5.opExtrude","SWEPT_FACE",FACE,{"disambiguationData":[OSD([sQuery(id+"F4.wireOp",EDGE,"E31")])]})]})]});
            var Q7;
            Q7=makeQuery(id+"F8.opChamfer","BLEND_EDGE",EDGE,{"blendedFrom":[makeQuery(id+"F1.opExtrude","CAP_EDGE",EDGE,{"disambiguationData":[OSD([sQuery(id+"F0.wireOp",EDGE,"E1")])],"isStart":false}),makeQuery(id+"F5.boolean.opBoolean","MERGE",FACE,{"derivedFrom":[makeQuery(id+"F1.opExtrude","SWEPT_FACE",FACE,{"disambiguationData":[OSD([sQuery(id+"F0.wireOp",EDGE,"E11")])]}),makeQuery(id+"F5.opExtrude","SWEPT_FACE",FACE,{"disambiguationData":[OSD([sQuery(id+"F4.wireOp",EDGE,"E32")])]})]})],"blendedInto":[makeQuery(id+"F5.boolean.opBoolean","MERGE",FACE,{"derivedFrom":[makeQuery(id+"F1.opExtrude","SWEPT_FACE",FACE,{"disambiguationData":[OSD([sQuery(id+"F0.wireOp",EDGE,"E11")])]}),makeQuery(id+"F5.opExtrude","SWEPT_FACE",FACE,{"disambiguationData":[OSD([sQuery(id+"F4.wireOp",EDGE,"E32")])]})]})]});
            fillet(context, id + "F13", {"entities" : qUnion([Q0, Q1, Q2, Q3, Q4, Q5, Q6, Q7]), "radius" : 7 * mm, "tangentPropagation" : true, "allowEdgeOverflow" : false});
        }
        {
            var Q0;
            {var subQ0=sQuery(id+"F0.wireOp",EDGE,"E1");var subQ1=sQuery(id+"F0.wireOp",EDGE,"E0");var subQ2=makeQuery(id+"F1.opExtrude","CAP_FACE",FACE,{"disambiguationData":[OSD([subQ1,subQ0,sQuery(id+"F0.wireOp",EDGE,"E2"),sQuery(id+"F0.wireOp",EDGE,"E3"),sQuery(id+"F0.wireOp",EDGE,"E4"),sQuery(id+"F0.wireOp",EDGE,"E5"),sQuery(id+"F0.wireOp",EDGE,"E6"),sQuery(id+"F0.wireOp",EDGE,"E7"),sQuery(id+"F0.wireOp",EDGE,"E8"),sQuery(id+"F0.wireOp",EDGE,"E9"),sQuery(id+"F0.wireOp",EDGE,"E10"),sQuery(id+"F0.wireOp",EDGE,"E11"),sQuery(id+"F0.wireOp",EDGE,"E12"),sQuery(id+"F0.wireOp",EDGE,"E13"),sQuery(id+"F0.wireOp",EDGE,"E14"),sQuery(id+"F0.wireOp",EDGE,"E15"),sQuery(id+"F0.wireOp",EDGE,"E16"),sQuery(id+"F0.wireOp",EDGE,"E17"),sQuery(id+"F0.wireOp",EDGE,"E18"),sQuery(id+"F0.wireOp",EDGE,"E19"),sQuery(id+"F0.wireOp",EDGE,"E20"),sQuery(id+"F0.wireOp",EDGE,"E21"),sQuery(id+"F0.wireOp",EDGE,"E22.filletArc"),sQuery(id+"F0.wireOp",EDGE,"E23.filletArc"),sQuery(id+"F0.wireOp",EDGE,"E24.filletArc"),sQuery(id+"F0.wireOp",EDGE,"E25.filletArc"),sQuery(id+"F0.wireOp",EDGE,"E26.filletArc"),sQuery(id+"F0.wireOp",EDGE,"E27.filletArc"),sQuery(id+"F0.wireOp",EDGE,"E28.filletArc"),sQuery(id+"F0.wireOp",EDGE,"E29.filletArc")])],"isStart":false});Q0=makeQuery(id+"F8.opChamfer","BLEND_EDGE",EDGE,{"blendedFrom":[makeQuery(id+"F6.opFillet","BLEND_EDGE",EDGE,{"blendedFrom":[makeQuery(id+"F1.opExtrude","SWEPT_EDGE",EDGE,{"disambiguationData":[OSD([subQ1,subQ0])]}),subQ2],"blendedInto":[subQ2]}),subQ2],"blendedInto":[subQ2]});}
            var Q1;
            {var subQ0=sQuery(id+"F0.wireOp",EDGE,"E5");var subQ1=sQuery(id+"F0.wireOp",EDGE,"E4");var subQ2=makeQuery(id+"F1.opExtrude","CAP_FACE",FACE,{"disambiguationData":[OSD([sQuery(id+"F0.wireOp",EDGE,"E0"),sQuery(id+"F0.wireOp",EDGE,"E1"),sQuery(id+"F0.wireOp",EDGE,"E2"),sQuery(id+"F0.wireOp",EDGE,"E3"),subQ1,subQ0,sQuery(id+"F0.wireOp",EDGE,"E6"),sQuery(id+"F0.wireOp",EDGE,"E7"),sQuery(id+"F0.wireOp",EDGE,"E8"),sQuery(id+"F0.wireOp",EDGE,"E9"),sQuery(id+"F0.wireOp",EDGE,"E10"),sQuery(id+"F0.wireOp",EDGE,"E11"),sQuery(id+"F0.wireOp",EDGE,"E12"),sQuery(id+"F0.wireOp",EDGE,"E13"),sQuery(id+"F0.wireOp",EDGE,"E14"),sQuery(id+"F0.wireOp",EDGE,"E15"),sQuery(id+"F0.wireOp",EDGE,"E16"),sQuery(id+"F0.wireOp",EDGE,"E17"),sQuery(id+"F0.wireOp",EDGE,"E18"),sQuery(id+"F0.wireOp",EDGE,"E19"),sQuery(id+"F0.wireOp",EDGE,"E20"),sQuery(id+"F0.wireOp",EDGE,"E21"),sQuery(id+"F0.wireOp",EDGE,"E22.filletArc"),sQuery(id+"F0.wireOp",EDGE,"E23.filletArc"),sQuery(id+"F0.wireOp",EDGE,"E24.filletArc"),sQuery(id+"F0.wireOp",EDGE,"E25.filletArc"),sQuery(id+"F0.wireOp",EDGE,"E26.filletArc"),sQuery(id+"F0.wireOp",EDGE,"E27.filletArc"),sQuery(id+"F0.wireOp",EDGE,"E28.filletArc"),sQuery(id+"F0.wireOp",EDGE,"E29.filletArc")])],"isStart":false});Q1=makeQuery(id+"F8.opChamfer","BLEND_EDGE",EDGE,{"blendedFrom":[makeQuery(id+"F7.opFillet","BLEND_EDGE",EDGE,{"blendedFrom":[makeQuery(id+"F1.opExtrude","SWEPT_EDGE",EDGE,{"disambiguationData":[OSD([subQ1,subQ0])]}),subQ2],"blendedInto":[subQ2]}),subQ2],"blendedInto":[subQ2]});}
            var Q2;
            {var subQ0=sQuery(id+"F0.wireOp",EDGE,"E3");var subQ1=sQuery(id+"F0.wireOp",EDGE,"E2");var subQ2=makeQuery(id+"F1.opExtrude","CAP_FACE",FACE,{"disambiguationData":[OSD([sQuery(id+"F0.wireOp",EDGE,"E0"),sQuery(id+"F0.wireOp",EDGE,"E1"),subQ1,subQ0,sQuery(id+"F0.wireOp",EDGE,"E4"),sQuery(id+"F0.wireOp",EDGE,"E5"),sQuery(id+"F0.wireOp",EDGE,"E6"),sQuery(id+"F0.wireOp",EDGE,"E7"),sQuery(id+"F0.wireOp",EDGE,"E8"),sQuery(id+"F0.wireOp",EDGE,"E9"),sQuery(id+"F0.wireOp",EDGE,"E10"),sQuery(id+"F0.wireOp",EDGE,"E11"),sQuery(id+"F0.wireOp",EDGE,"E12"),sQuery(id+"F0.wireOp",EDGE,"E13"),sQuery(id+"F0.wireOp",EDGE,"E14"),sQuery(id+"F0.wireOp",EDGE,"E15"),sQuery(id+"F0.wireOp",EDGE,"E16"),sQuery(id+"F0.wireOp",EDGE,"E17"),sQuery(id+"F0.wireOp",EDGE,"E18"),sQuery(id+"F0.wireOp",EDGE,"E19"),sQuery(id+"F0.wireOp",EDGE,"E20"),sQuery(id+"F0.wireOp",EDGE,"E21"),sQuery(id+"F0.wireOp",EDGE,"E22.filletArc"),sQuery(id+"F0.wireOp",EDGE,"E23.filletArc"),sQuery(id+"F0.wireOp",EDGE,"E24.filletArc"),sQuery(id+"F0.wireOp",EDGE,"E25.filletArc"),sQuery(id+"F0.wireOp",EDGE,"E26.filletArc"),sQuery(id+"F0.wireOp",EDGE,"E27.filletArc"),sQuery(id+"F0.wireOp",EDGE,"E28.filletArc"),sQuery(id+"F0.wireOp",EDGE,"E29.filletArc")])],"isStart":false});Q2=makeQuery(id+"F8.opChamfer","BLEND_EDGE",EDGE,{"blendedFrom":[makeQuery(id+"F6.opFillet","BLEND_EDGE",EDGE,{"blendedFrom":[makeQuery(id+"F1.opExtrude","SWEPT_EDGE",EDGE,{"disambiguationData":[OSD([subQ1,subQ0])]}),subQ2],"blendedInto":[subQ2]}),subQ2],"blendedInto":[subQ2]});}
            var Q3;
            {var subQ0=sQuery(id+"F0.wireOp",EDGE,"E8");Q3=makeQuery(id+"F8.opChamfer","BLEND_EDGE",EDGE,{"blendedFrom":[makeQuery(id+"F1.opExtrude","CAP_EDGE",EDGE,{"disambiguationData":[OSD([subQ0])],"isStart":false}),makeQuery(id+"F1.opExtrude","CAP_FACE",FACE,{"disambiguationData":[OSD([sQuery(id+"F0.wireOp",EDGE,"E0"),sQuery(id+"F0.wireOp",EDGE,"E1"),sQuery(id+"F0.wireOp",EDGE,"E2"),sQuery(id+"F0.wireOp",EDGE,"E3"),sQuery(id+"F0.wireOp",EDGE,"E4"),sQuery(id+"F0.wireOp",EDGE,"E5"),sQuery(id+"F0.wireOp",EDGE,"E6"),sQuery(id+"F0.wireOp",EDGE,"E7"),subQ0,sQuery(id+"F0.wireOp",EDGE,"E9"),sQuery(id+"F0.wireOp",EDGE,"E10"),sQuery(id+"F0.wireOp",EDGE,"E11"),sQuery(id+"F0.wireOp",EDGE,"E12"),sQuery(id+"F0.wireOp",EDGE,"E13"),sQuery(id+"F0.wireOp",EDGE,"E14"),sQuery(id+"F0.wireOp",EDGE,"E15"),sQuery(id+"F0.wireOp",EDGE,"E16"),sQuery(id+"F0.wireOp",EDGE,"E17"),sQuery(id+"F0.wireOp",EDGE,"E18"),sQuery(id+"F0.wireOp",EDGE,"E19"),sQuery(id+"F0.wireOp",EDGE,"E20"),sQuery(id+"F0.wireOp",EDGE,"E21"),sQuery(id+"F0.wireOp",EDGE,"E22.filletArc"),sQuery(id+"F0.wireOp",EDGE,"E23.filletArc"),sQuery(id+"F0.wireOp",EDGE,"E24.filletArc"),sQuery(id+"F0.wireOp",EDGE,"E25.filletArc"),sQuery(id+"F0.wireOp",EDGE,"E26.filletArc"),sQuery(id+"F0.wireOp",EDGE,"E27.filletArc"),sQuery(id+"F0.wireOp",EDGE,"E28.filletArc"),sQuery(id+"F0.wireOp",EDGE,"E29.filletArc")])],"isStart":false})],"blendedInto":[makeQuery(id+"F1.opExtrude","CAP_FACE",FACE,{"disambiguationData":[OSD([sQuery(id+"F0.wireOp",EDGE,"E0"),sQuery(id+"F0.wireOp",EDGE,"E1"),sQuery(id+"F0.wireOp",EDGE,"E2"),sQuery(id+"F0.wireOp",EDGE,"E3"),sQuery(id+"F0.wireOp",EDGE,"E4"),sQuery(id+"F0.wireOp",EDGE,"E5"),sQuery(id+"F0.wireOp",EDGE,"E6"),sQuery(id+"F0.wireOp",EDGE,"E7"),subQ0,sQuery(id+"F0.wireOp",EDGE,"E9"),sQuery(id+"F0.wireOp",EDGE,"E10"),sQuery(id+"F0.wireOp",EDGE,"E11"),sQuery(id+"F0.wireOp",EDGE,"E12"),sQuery(id+"F0.wireOp",EDGE,"E13"),sQuery(id+"F0.wireOp",EDGE,"E14"),sQuery(id+"F0.wireOp",EDGE,"E15"),sQuery(id+"F0.wireOp",EDGE,"E16"),sQuery(id+"F0.wireOp",EDGE,"E17"),sQuery(id+"F0.wireOp",EDGE,"E18"),sQuery(id+"F0.wireOp",EDGE,"E19"),sQuery(id+"F0.wireOp",EDGE,"E20"),sQuery(id+"F0.wireOp",EDGE,"E21"),sQuery(id+"F0.wireOp",EDGE,"E22.filletArc"),sQuery(id+"F0.wireOp",EDGE,"E23.filletArc"),sQuery(id+"F0.wireOp",EDGE,"E24.filletArc"),sQuery(id+"F0.wireOp",EDGE,"E25.filletArc"),sQuery(id+"F0.wireOp",EDGE,"E26.filletArc"),sQuery(id+"F0.wireOp",EDGE,"E27.filletArc"),sQuery(id+"F0.wireOp",EDGE,"E28.filletArc"),sQuery(id+"F0.wireOp",EDGE,"E29.filletArc")])],"isStart":false})]});}
            fillet(context, id + "F14", {"entities" : qUnion([Q0, Q1, Q2, Q3]), "radius" : .7 * mm, "tangentPropagation" : true, "allowEdgeOverflow" : false});
        }
        {
            var Q0;
            {var subQ0=makeQuery(id+"F1.opExtrude","CAP_FACE",FACE,{"disambiguationData":[OSD([sQuery(id+"F0.wireOp",EDGE,"E0"),sQuery(id+"F0.wireOp",EDGE,"E1"),sQuery(id+"F0.wireOp",EDGE,"E2"),sQuery(id+"F0.wireOp",EDGE,"E3"),sQuery(id+"F0.wireOp",EDGE,"E4"),sQuery(id+"F0.wireOp",EDGE,"E5"),sQuery(id+"F0.wireOp",EDGE,"E6"),sQuery(id+"F0.wireOp",EDGE,"E7"),sQuery(id+"F0.wireOp",EDGE,"E8"),sQuery(id+"F0.wireOp",EDGE,"E9"),sQuery(id+"F0.wireOp",EDGE,"E10"),sQuery(id+"F0.wireOp",EDGE,"E11"),sQuery(id+"F0.wireOp",EDGE,"E12"),sQuery(id+"F0.wireOp",EDGE,"E13"),sQuery(id+"F0.wireOp",EDGE,"E14"),sQuery(id+"F0.wireOp",EDGE,"E15"),sQuery(id+"F0.wireOp",EDGE,"E16"),sQuery(id+"F0.wireOp",EDGE,"E17"),sQuery(id+"F0.wireOp",EDGE,"E18"),sQuery(id+"F0.wireOp",EDGE,"E19"),sQuery(id+"F0.wireOp",EDGE,"E20"),sQuery(id+"F0.wireOp",EDGE,"E21"),sQuery(id+"F0.wireOp",EDGE,"E22.filletArc"),sQuery(id+"F0.wireOp",EDGE,"E23.filletArc"),sQuery(id+"F0.wireOp",EDGE,"E24.filletArc"),sQuery(id+"F0.wireOp",EDGE,"E25.filletArc"),sQuery(id+"F0.wireOp",EDGE,"E26.filletArc"),sQuery(id+"F0.wireOp",EDGE,"E27.filletArc"),sQuery(id+"F0.wireOp",EDGE,"E28.filletArc"),sQuery(id+"F0.wireOp",EDGE,"E29.filletArc")])],"isStart":false});Q0=makeQuery(id+"F10.opChamfer","BLEND_EDGE",EDGE,{"blendedFrom":[makeQuery(id+"F3.boolean.opBoolean","INTERSECT",EDGE,{"derivedFrom":[subQ0,makeQuery(id+"F3.opExtrude","CAP_FACE",FACE,{"disambiguationData":[OSD([sQuery(id+"F2.wireOp",EDGE,"E30.bottom"),sQuery(id+"F2.wireOp",EDGE,"E30.top"),sQuery(id+"F2.wireOp",EDGE,"E30.left"),sQuery(id+"F2.wireOp",EDGE,"E30.right")])],"isStart":false})]}),subQ0],"blendedInto":[subQ0]});}
            fillet(context, id + "F15", {"entities" : qUnion([Q0]), "radius" : .7 * mm, "tangentPropagation" : true, "allowEdgeOverflow" : false});
        }
        {
            var Q0;
            {var subQ0=sQuery(id+"F2.wireOp",EDGE,"E30.top");Q0=makeQuery(id+"F10.opChamfer","BLEND_EDGE",EDGE,{"blendedFrom":[makeQuery(id+"F3.boolean.opBoolean","INTERSECT",EDGE,{"derivedFrom":[makeQuery(id+"F1.opExtrude","CAP_FACE",FACE,{"disambiguationData":[OSD([sQuery(id+"F0.wireOp",EDGE,"E0"),sQuery(id+"F0.wireOp",EDGE,"E1"),sQuery(id+"F0.wireOp",EDGE,"E2"),sQuery(id+"F0.wireOp",EDGE,"E3"),sQuery(id+"F0.wireOp",EDGE,"E4"),sQuery(id+"F0.wireOp",EDGE,"E5"),sQuery(id+"F0.wireOp",EDGE,"E6"),sQuery(id+"F0.wireOp",EDGE,"E7"),sQuery(id+"F0.wireOp",EDGE,"E8"),sQuery(id+"F0.wireOp",EDGE,"E9"),sQuery(id+"F0.wireOp",EDGE,"E10"),sQuery(id+"F0.wireOp",EDGE,"E11"),sQuery(id+"F0.wireOp",EDGE,"E12"),sQuery(id+"F0.wireOp",EDGE,"E13"),sQuery(id+"F0.wireOp",EDGE,"E14"),sQuery(id+"F0.wireOp",EDGE,"E15"),sQuery(id+"F0.wireOp",EDGE,"E16"),sQuery(id+"F0.wireOp",EDGE,"E17"),sQuery(id+"F0.wireOp",EDGE,"E18"),sQuery(id+"F0.wireOp",EDGE,"E19"),sQuery(id+"F0.wireOp",EDGE,"E20"),sQuery(id+"F0.wireOp",EDGE,"E21"),sQuery(id+"F0.wireOp",EDGE,"E22.filletArc"),sQuery(id+"F0.wireOp",EDGE,"E23.filletArc"),sQuery(id+"F0.wireOp",EDGE,"E24.filletArc"),sQuery(id+"F0.wireOp",EDGE,"E25.filletArc"),sQuery(id+"F0.wireOp",EDGE,"E26.filletArc"),sQuery(id+"F0.wireOp",EDGE,"E27.filletArc"),sQuery(id+"F0.wireOp",EDGE,"E28.filletArc"),sQuery(id+"F0.wireOp",EDGE,"E29.filletArc")])],"isStart":false}),makeQuery(id+"F3.opExtrude","CAP_FACE",FACE,{"disambiguationData":[OSD([sQuery(id+"F2.wireOp",EDGE,"E30.bottom"),subQ0,sQuery(id+"F2.wireOp",EDGE,"E30.left"),sQuery(id+"F2.wireOp",EDGE,"E30.right")])],"isStart":false})]}),makeQuery(id+"F3.boolean.opBoolean","COPY",FACE,{"derivedFrom":makeQuery(id+"F3.opExtrude","SWEPT_FACE",FACE,{"disambiguationData":[OSD([subQ0])]})})],"blendedInto":[makeQuery(id+"F3.boolean.opBoolean","COPY",FACE,{"derivedFrom":makeQuery(id+"F3.opExtrude","SWEPT_FACE",FACE,{"disambiguationData":[OSD([subQ0])]})})]});}
            fillet(context, id + "F16", {"entities" : qUnion([Q0]), "radius" : 1.5 * mm, "tangentPropagation" : true, "allowEdgeOverflow" : false});
        }
        {
            var Q0;
            Q0=makeQuery(id+"F5.opExtrude","CAP_EDGE",EDGE,{"disambiguationData":[OSD([sQuery(id+"F4.wireOp",EDGE,"E31")])],"isStart":false});
            var Q1;
            Q1=makeQuery(id+"F5.opExtrude","CAP_FACE",FACE,{"disambiguationData":[OSD([sQuery(id+"F4.wireOp",EDGE,"E32")])],"isStart":false});
            var Q2;
            Q2=makeQuery(id+"F5.opExtrude","CAP_FACE",FACE,{"disambiguationData":[OSD([sQuery(id+"F4.wireOp",EDGE,"E33")])],"isStart":false});
            var Q3;
            Q3=makeQuery(id+"F5.opExtrude","CAP_EDGE",EDGE,{"disambiguationData":[OSD([sQuery(id+"F4.wireOp",EDGE,"E34")])],"isStart":false});
            fillet(context, id + "F17", {"entities" : qUnion([Q0, Q1, Q2, Q3]), "radius" : 1.4 * mm, "tangentPropagation" : true, "allowEdgeOverflow" : false});
        }
        {
            var Q0;
            Q0=makeQuery(id+"F17.opFillet","BLEND_EDGE",EDGE,{"blendedFrom":[makeQuery(id+"F5.opExtrude","CAP_EDGE",EDGE,{"disambiguationData":[OSD([sQuery(id+"F4.wireOp",EDGE,"E31")])],"isStart":false}),makeQuery(id+"F1.opExtrude","CAP_FACE",FACE,{"disambiguationData":[OSD([sQuery(id+"F0.wireOp",EDGE,"E0"),sQuery(id+"F0.wireOp",EDGE,"E1"),sQuery(id+"F0.wireOp",EDGE,"E2"),sQuery(id+"F0.wireOp",EDGE,"E3"),sQuery(id+"F0.wireOp",EDGE,"E4"),sQuery(id+"F0.wireOp",EDGE,"E5"),sQuery(id+"F0.wireOp",EDGE,"E6"),sQuery(id+"F0.wireOp",EDGE,"E7"),sQuery(id+"F0.wireOp",EDGE,"E8"),sQuery(id+"F0.wireOp",EDGE,"E9"),sQuery(id+"F0.wireOp",EDGE,"E10"),sQuery(id+"F0.wireOp",EDGE,"E11"),sQuery(id+"F0.wireOp",EDGE,"E12"),sQuery(id+"F0.wireOp",EDGE,"E13"),sQuery(id+"F0.wireOp",EDGE,"E14"),sQuery(id+"F0.wireOp",EDGE,"E15"),sQuery(id+"F0.wireOp",EDGE,"E16"),sQuery(id+"F0.wireOp",EDGE,"E17"),sQuery(id+"F0.wireOp",EDGE,"E18"),sQuery(id+"F0.wireOp",EDGE,"E19"),sQuery(id+"F0.wireOp",EDGE,"E20"),sQuery(id+"F0.wireOp",EDGE,"E21"),sQuery(id+"F0.wireOp",EDGE,"E22.filletArc"),sQuery(id+"F0.wireOp",EDGE,"E23.filletArc"),sQuery(id+"F0.wireOp",EDGE,"E24.filletArc"),sQuery(id+"F0.wireOp",EDGE,"E25.filletArc"),sQuery(id+"F0.wireOp",EDGE,"E26.filletArc"),sQuery(id+"F0.wireOp",EDGE,"E27.filletArc"),sQuery(id+"F0.wireOp",EDGE,"E28.filletArc"),sQuery(id+"F0.wireOp",EDGE,"E29.filletArc")])],"isStart":false})],"blendedInto":[makeQuery(id+"F1.opExtrude","CAP_FACE",FACE,{"disambiguationData":[OSD([sQuery(id+"F0.wireOp",EDGE,"E0"),sQuery(id+"F0.wireOp",EDGE,"E1"),sQuery(id+"F0.wireOp",EDGE,"E2"),sQuery(id+"F0.wireOp",EDGE,"E3"),sQuery(id+"F0.wireOp",EDGE,"E4"),sQuery(id+"F0.wireOp",EDGE,"E5"),sQuery(id+"F0.wireOp",EDGE,"E6"),sQuery(id+"F0.wireOp",EDGE,"E7"),sQuery(id+"F0.wireOp",EDGE,"E8"),sQuery(id+"F0.wireOp",EDGE,"E9"),sQuery(id+"F0.wireOp",EDGE,"E10"),sQuery(id+"F0.wireOp",EDGE,"E11"),sQuery(id+"F0.wireOp",EDGE,"E12"),sQuery(id+"F0.wireOp",EDGE,"E13"),sQuery(id+"F0.wireOp",EDGE,"E14"),sQuery(id+"F0.wireOp",EDGE,"E15"),sQuery(id+"F0.wireOp",EDGE,"E16"),sQuery(id+"F0.wireOp",EDGE,"E17"),sQuery(id+"F0.wireOp",EDGE,"E18"),sQuery(id+"F0.wireOp",EDGE,"E19"),sQuery(id+"F0.wireOp",EDGE,"E20"),sQuery(id+"F0.wireOp",EDGE,"E21"),sQuery(id+"F0.wireOp",EDGE,"E22.filletArc"),sQuery(id+"F0.wireOp",EDGE,"E23.filletArc"),sQuery(id+"F0.wireOp",EDGE,"E24.filletArc"),sQuery(id+"F0.wireOp",EDGE,"E25.filletArc"),sQuery(id+"F0.wireOp",EDGE,"E26.filletArc"),sQuery(id+"F0.wireOp",EDGE,"E27.filletArc"),sQuery(id+"F0.wireOp",EDGE,"E28.filletArc"),sQuery(id+"F0.wireOp",EDGE,"E29.filletArc")])],"isStart":false})]});
            var Q1;
            Q1=makeQuery(id+"F17.opFillet","BLEND_EDGE",EDGE,{"blendedFrom":[makeQuery(id+"F5.opExtrude","CAP_EDGE",EDGE,{"disambiguationData":[OSD([sQuery(id+"F4.wireOp",EDGE,"E34")])],"isStart":false}),makeQuery(id+"F1.opExtrude","CAP_FACE",FACE,{"disambiguationData":[OSD([sQuery(id+"F0.wireOp",EDGE,"E0"),sQuery(id+"F0.wireOp",EDGE,"E1"),sQuery(id+"F0.wireOp",EDGE,"E2"),sQuery(id+"F0.wireOp",EDGE,"E3"),sQuery(id+"F0.wireOp",EDGE,"E4"),sQuery(id+"F0.wireOp",EDGE,"E5"),sQuery(id+"F0.wireOp",EDGE,"E6"),sQuery(id+"F0.wireOp",EDGE,"E7"),sQuery(id+"F0.wireOp",EDGE,"E8"),sQuery(id+"F0.wireOp",EDGE,"E9"),sQuery(id+"F0.wireOp",EDGE,"E10"),sQuery(id+"F0.wireOp",EDGE,"E11"),sQuery(id+"F0.wireOp",EDGE,"E12"),sQuery(id+"F0.wireOp",EDGE,"E13"),sQuery(id+"F0.wireOp",EDGE,"E14"),sQuery(id+"F0.wireOp",EDGE,"E15"),sQuery(id+"F0.wireOp",EDGE,"E16"),sQuery(id+"F0.wireOp",EDGE,"E17"),sQuery(id+"F0.wireOp",EDGE,"E18"),sQuery(id+"F0.wireOp",EDGE,"E19"),sQuery(id+"F0.wireOp",EDGE,"E20"),sQuery(id+"F0.wireOp",EDGE,"E21"),sQuery(id+"F0.wireOp",EDGE,"E22.filletArc"),sQuery(id+"F0.wireOp",EDGE,"E23.filletArc"),sQuery(id+"F0.wireOp",EDGE,"E24.filletArc"),sQuery(id+"F0.wireOp",EDGE,"E25.filletArc"),sQuery(id+"F0.wireOp",EDGE,"E26.filletArc"),sQuery(id+"F0.wireOp",EDGE,"E27.filletArc"),sQuery(id+"F0.wireOp",EDGE,"E28.filletArc"),sQuery(id+"F0.wireOp",EDGE,"E29.filletArc")])],"isStart":false})],"blendedInto":[makeQuery(id+"F1.opExtrude","CAP_FACE",FACE,{"disambiguationData":[OSD([sQuery(id+"F0.wireOp",EDGE,"E0"),sQuery(id+"F0.wireOp",EDGE,"E1"),sQuery(id+"F0.wireOp",EDGE,"E2"),sQuery(id+"F0.wireOp",EDGE,"E3"),sQuery(id+"F0.wireOp",EDGE,"E4"),sQuery(id+"F0.wireOp",EDGE,"E5"),sQuery(id+"F0.wireOp",EDGE,"E6"),sQuery(id+"F0.wireOp",EDGE,"E7"),sQuery(id+"F0.wireOp",EDGE,"E8"),sQuery(id+"F0.wireOp",EDGE,"E9"),sQuery(id+"F0.wireOp",EDGE,"E10"),sQuery(id+"F0.wireOp",EDGE,"E11"),sQuery(id+"F0.wireOp",EDGE,"E12"),sQuery(id+"F0.wireOp",EDGE,"E13"),sQuery(id+"F0.wireOp",EDGE,"E14"),sQuery(id+"F0.wireOp",EDGE,"E15"),sQuery(id+"F0.wireOp",EDGE,"E16"),sQuery(id+"F0.wireOp",EDGE,"E17"),sQuery(id+"F0.wireOp",EDGE,"E18"),sQuery(id+"F0.wireOp",EDGE,"E19"),sQuery(id+"F0.wireOp",EDGE,"E20"),sQuery(id+"F0.wireOp",EDGE,"E21"),sQuery(id+"F0.wireOp",EDGE,"E22.filletArc"),sQuery(id+"F0.wireOp",EDGE,"E23.filletArc"),sQuery(id+"F0.wireOp",EDGE,"E24.filletArc"),sQuery(id+"F0.wireOp",EDGE,"E25.filletArc"),sQuery(id+"F0.wireOp",EDGE,"E26.filletArc"),sQuery(id+"F0.wireOp",EDGE,"E27.filletArc"),sQuery(id+"F0.wireOp",EDGE,"E28.filletArc"),sQuery(id+"F0.wireOp",EDGE,"E29.filletArc")])],"isStart":false})]});
            var Q2;
            Q2=makeQuery(id+"F17.opFillet","BLEND_EDGE",EDGE,{"blendedFrom":[makeQuery(id+"F5.opExtrude","CAP_EDGE",EDGE,{"disambiguationData":[OSD([sQuery(id+"F4.wireOp",EDGE,"E33")])],"isStart":false}),makeQuery(id+"F1.opExtrude","CAP_FACE",FACE,{"disambiguationData":[OSD([sQuery(id+"F0.wireOp",EDGE,"E0"),sQuery(id+"F0.wireOp",EDGE,"E1"),sQuery(id+"F0.wireOp",EDGE,"E2"),sQuery(id+"F0.wireOp",EDGE,"E3"),sQuery(id+"F0.wireOp",EDGE,"E4"),sQuery(id+"F0.wireOp",EDGE,"E5"),sQuery(id+"F0.wireOp",EDGE,"E6"),sQuery(id+"F0.wireOp",EDGE,"E7"),sQuery(id+"F0.wireOp",EDGE,"E8"),sQuery(id+"F0.wireOp",EDGE,"E9"),sQuery(id+"F0.wireOp",EDGE,"E10"),sQuery(id+"F0.wireOp",EDGE,"E11"),sQuery(id+"F0.wireOp",EDGE,"E12"),sQuery(id+"F0.wireOp",EDGE,"E13"),sQuery(id+"F0.wireOp",EDGE,"E14"),sQuery(id+"F0.wireOp",EDGE,"E15"),sQuery(id+"F0.wireOp",EDGE,"E16"),sQuery(id+"F0.wireOp",EDGE,"E17"),sQuery(id+"F0.wireOp",EDGE,"E18"),sQuery(id+"F0.wireOp",EDGE,"E19"),sQuery(id+"F0.wireOp",EDGE,"E20"),sQuery(id+"F0.wireOp",EDGE,"E21"),sQuery(id+"F0.wireOp",EDGE,"E22.filletArc"),sQuery(id+"F0.wireOp",EDGE,"E23.filletArc"),sQuery(id+"F0.wireOp",EDGE,"E24.filletArc"),sQuery(id+"F0.wireOp",EDGE,"E25.filletArc"),sQuery(id+"F0.wireOp",EDGE,"E26.filletArc"),sQuery(id+"F0.wireOp",EDGE,"E27.filletArc"),sQuery(id+"F0.wireOp",EDGE,"E28.filletArc"),sQuery(id+"F0.wireOp",EDGE,"E29.filletArc")])],"isStart":false})],"blendedInto":[makeQuery(id+"F1.opExtrude","CAP_FACE",FACE,{"disambiguationData":[OSD([sQuery(id+"F0.wireOp",EDGE,"E0"),sQuery(id+"F0.wireOp",EDGE,"E1"),sQuery(id+"F0.wireOp",EDGE,"E2"),sQuery(id+"F0.wireOp",EDGE,"E3"),sQuery(id+"F0.wireOp",EDGE,"E4"),sQuery(id+"F0.wireOp",EDGE,"E5"),sQuery(id+"F0.wireOp",EDGE,"E6"),sQuery(id+"F0.wireOp",EDGE,"E7"),sQuery(id+"F0.wireOp",EDGE,"E8"),sQuery(id+"F0.wireOp",EDGE,"E9"),sQuery(id+"F0.wireOp",EDGE,"E10"),sQuery(id+"F0.wireOp",EDGE,"E11"),sQuery(id+"F0.wireOp",EDGE,"E12"),sQuery(id+"F0.wireOp",EDGE,"E13"),sQuery(id+"F0.wireOp",EDGE,"E14"),sQuery(id+"F0.wireOp",EDGE,"E15"),sQuery(id+"F0.wireOp",EDGE,"E16"),sQuery(id+"F0.wireOp",EDGE,"E17"),sQuery(id+"F0.wireOp",EDGE,"E18"),sQuery(id+"F0.wireOp",EDGE,"E19"),sQuery(id+"F0.wireOp",EDGE,"E20"),sQuery(id+"F0.wireOp",EDGE,"E21"),sQuery(id+"F0.wireOp",EDGE,"E22.filletArc"),sQuery(id+"F0.wireOp",EDGE,"E23.filletArc"),sQuery(id+"F0.wireOp",EDGE,"E24.filletArc"),sQuery(id+"F0.wireOp",EDGE,"E25.filletArc"),sQuery(id+"F0.wireOp",EDGE,"E26.filletArc"),sQuery(id+"F0.wireOp",EDGE,"E27.filletArc"),sQuery(id+"F0.wireOp",EDGE,"E28.filletArc"),sQuery(id+"F0.wireOp",EDGE,"E29.filletArc")])],"isStart":false})]});
            var Q3;
            Q3=makeQuery(id+"F17.opFillet","BLEND_EDGE",EDGE,{"blendedFrom":[makeQuery(id+"F5.opExtrude","CAP_EDGE",EDGE,{"disambiguationData":[OSD([sQuery(id+"F4.wireOp",EDGE,"E32")])],"isStart":false}),makeQuery(id+"F1.opExtrude","CAP_FACE",FACE,{"disambiguationData":[OSD([sQuery(id+"F0.wireOp",EDGE,"E0"),sQuery(id+"F0.wireOp",EDGE,"E1"),sQuery(id+"F0.wireOp",EDGE,"E2"),sQuery(id+"F0.wireOp",EDGE,"E3"),sQuery(id+"F0.wireOp",EDGE,"E4"),sQuery(id+"F0.wireOp",EDGE,"E5"),sQuery(id+"F0.wireOp",EDGE,"E6"),sQuery(id+"F0.wireOp",EDGE,"E7"),sQuery(id+"F0.wireOp",EDGE,"E8"),sQuery(id+"F0.wireOp",EDGE,"E9"),sQuery(id+"F0.wireOp",EDGE,"E10"),sQuery(id+"F0.wireOp",EDGE,"E11"),sQuery(id+"F0.wireOp",EDGE,"E12"),sQuery(id+"F0.wireOp",EDGE,"E13"),sQuery(id+"F0.wireOp",EDGE,"E14"),sQuery(id+"F0.wireOp",EDGE,"E15"),sQuery(id+"F0.wireOp",EDGE,"E16"),sQuery(id+"F0.wireOp",EDGE,"E17"),sQuery(id+"F0.wireOp",EDGE,"E18"),sQuery(id+"F0.wireOp",EDGE,"E19"),sQuery(id+"F0.wireOp",EDGE,"E20"),sQuery(id+"F0.wireOp",EDGE,"E21"),sQuery(id+"F0.wireOp",EDGE,"E22.filletArc"),sQuery(id+"F0.wireOp",EDGE,"E23.filletArc"),sQuery(id+"F0.wireOp",EDGE,"E24.filletArc"),sQuery(id+"F0.wireOp",EDGE,"E25.filletArc"),sQuery(id+"F0.wireOp",EDGE,"E26.filletArc"),sQuery(id+"F0.wireOp",EDGE,"E27.filletArc"),sQuery(id+"F0.wireOp",EDGE,"E28.filletArc"),sQuery(id+"F0.wireOp",EDGE,"E29.filletArc")])],"isStart":false})],"blendedInto":[makeQuery(id+"F1.opExtrude","CAP_FACE",FACE,{"disambiguationData":[OSD([sQuery(id+"F0.wireOp",EDGE,"E0"),sQuery(id+"F0.wireOp",EDGE,"E1"),sQuery(id+"F0.wireOp",EDGE,"E2"),sQuery(id+"F0.wireOp",EDGE,"E3"),sQuery(id+"F0.wireOp",EDGE,"E4"),sQuery(id+"F0.wireOp",EDGE,"E5"),sQuery(id+"F0.wireOp",EDGE,"E6"),sQuery(id+"F0.wireOp",EDGE,"E7"),sQuery(id+"F0.wireOp",EDGE,"E8"),sQuery(id+"F0.wireOp",EDGE,"E9"),sQuery(id+"F0.wireOp",EDGE,"E10"),sQuery(id+"F0.wireOp",EDGE,"E11"),sQuery(id+"F0.wireOp",EDGE,"E12"),sQuery(id+"F0.wireOp",EDGE,"E13"),sQuery(id+"F0.wireOp",EDGE,"E14"),sQuery(id+"F0.wireOp",EDGE,"E15"),sQuery(id+"F0.wireOp",EDGE,"E16"),sQuery(id+"F0.wireOp",EDGE,"E17"),sQuery(id+"F0.wireOp",EDGE,"E18"),sQuery(id+"F0.wireOp",EDGE,"E19"),sQuery(id+"F0.wireOp",EDGE,"E20"),sQuery(id+"F0.wireOp",EDGE,"E21"),sQuery(id+"F0.wireOp",EDGE,"E22.filletArc"),sQuery(id+"F0.wireOp",EDGE,"E23.filletArc"),sQuery(id+"F0.wireOp",EDGE,"E24.filletArc"),sQuery(id+"F0.wireOp",EDGE,"E25.filletArc"),sQuery(id+"F0.wireOp",EDGE,"E26.filletArc"),sQuery(id+"F0.wireOp",EDGE,"E27.filletArc"),sQuery(id+"F0.wireOp",EDGE,"E28.filletArc"),sQuery(id+"F0.wireOp",EDGE,"E29.filletArc")])],"isStart":false})]});
            fillet(context, id + "F18", {"entities" : qUnion([Q0, Q1, Q2, Q3]), "radius" : 5 * mm, "tangentPropagation" : true, "allowEdgeOverflow" : false});
        }
    });
